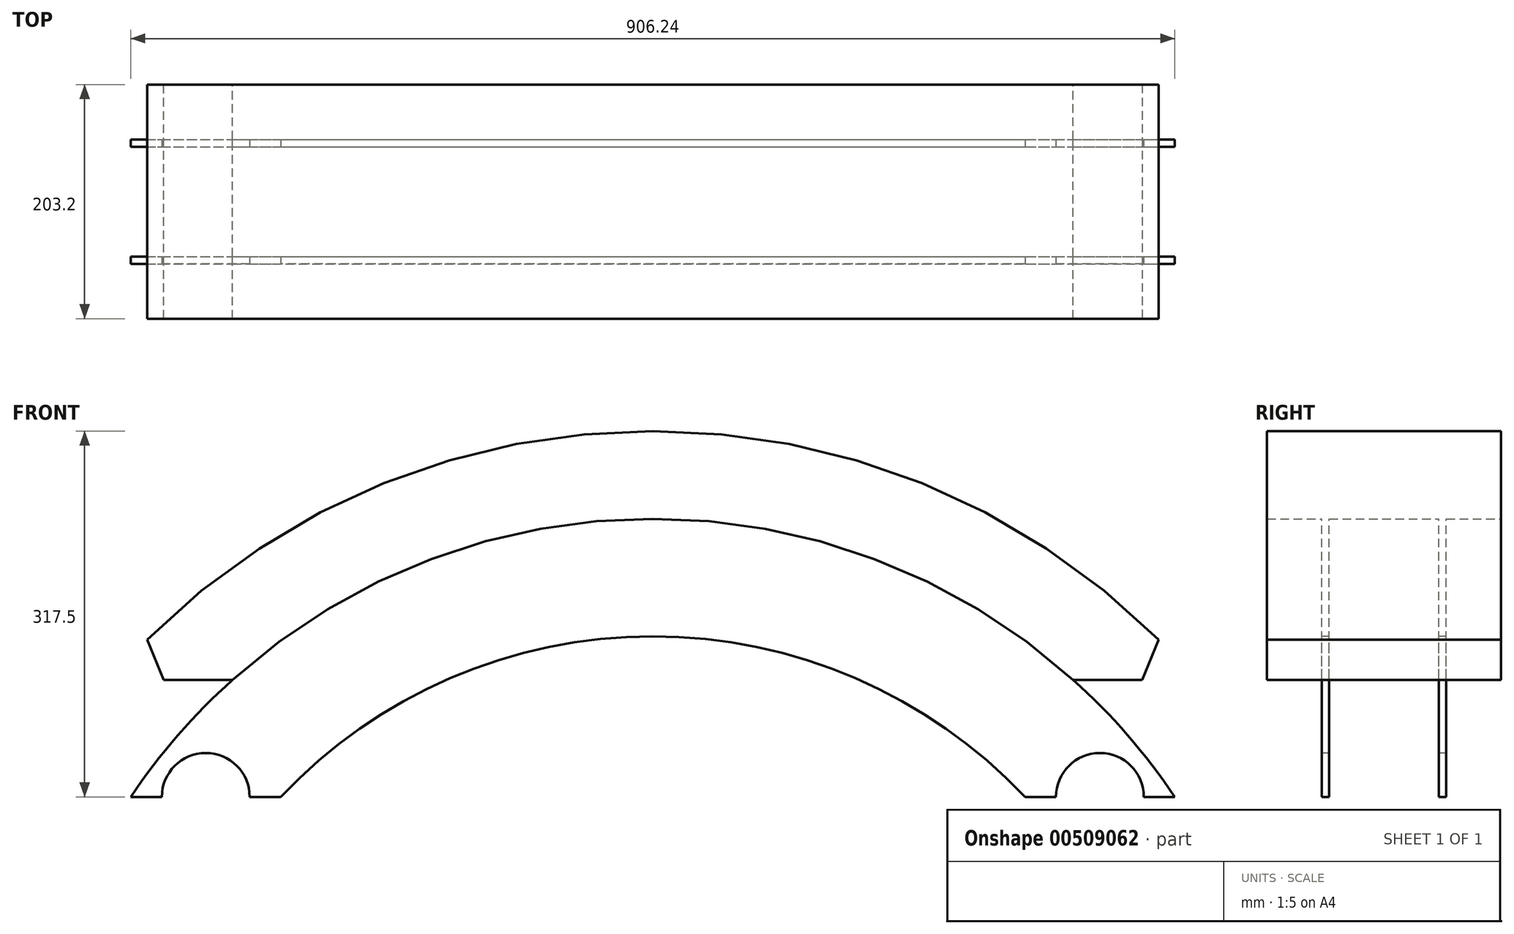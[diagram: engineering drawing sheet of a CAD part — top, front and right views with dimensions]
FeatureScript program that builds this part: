
annotation { "Feature Type Name" : "Feature", "Feature Type Description" : "" }
export const myFeature = defineFeature(function(context is Context, id is Id, definition is map)
    precondition{}
    {
        {
            var Q0;
            Q0=qCreatedBy(makeId("Front.planeOp"),FACE);
            var sketch = newSketch(context, id + "F0", { "sketchPlane" : qUnion([Q0])});
            skCircle(sketch, "E0", {"center": v(0, 0) * mm, "radius": 622.3 * mm});
            skCircle(sketch, "E1", {"center": v(0, 0) * mm, "radius": 546.1 * mm});
            skLineSegment(sketch, "E2.bottom", {"start": v(772.38, 406.4) * mm, "end": v(-772.38, 406.4) * mm});
            skLineSegment(sketch, "E2.top", {"start": v(772.38, -406.4) * mm, "end": v(-772.38, -406.4) * mm});
            skLineSegment(sketch, "E2.left", {"start": v(772.38, 406.4) * mm, "end": v(772.38, -406.4) * mm});
            skLineSegment(sketch, "E2.right", {"start": v(-772.38, 406.4) * mm, "end": v(-772.38, -406.4) * mm});
            skSolve(sketch);
        }
        {
            var Q0;
            {var subQ0=sQuery(id+"F0.wireOp",EDGE,"E2.bottom");var subQ1=sQuery(id+"F0.wireOp",EDGE,"E0");var subQ2=makeQuery(id+"F0.imprint","INTERSECT",VERTEX,{"disambiguationData":[OD(0.0)],"derivedFrom":[subQ1,subQ0]});Q0=makeQuery(id+"F0.imprint","IMPRINT",FACE,{"disambiguationData":[TD([[makeQuery(id+"F0.imprint","IMPRINT",EDGE,{"disambiguationData":[TD([[subQ2,1.0]])],"derivedFrom":subQ1}),1.0]])]});}
            extrude(context, id + "F1", {"entities" : qUnion([Q0]), "depth" : 203.2 * mm});
        }
        {
            var Q0;
            {var subQ0=sQuery(id+"F0.wireOp",EDGE,"E2.bottom");var subQ1=sQuery(id+"F0.wireOp",EDGE,"E0");Q0=makeQuery(id+"F1.opExtrude","SWEPT_EDGE",EDGE,{"disambiguationData":[OSD([subQ1,subQ0]),TDD([makeQuery(id+"F0.imprint","INTERSECT",VERTEX,{"disambiguationData":[OD(0.0)],"derivedFrom":[subQ1,subQ0]})])]});}
            var Q1;
            {var subQ0=sQuery(id+"F0.wireOp",EDGE,"E2.bottom");var subQ1=sQuery(id+"F0.wireOp",EDGE,"E0");Q1=makeQuery(id+"F1.opExtrude","SWEPT_EDGE",EDGE,{"disambiguationData":[OSD([subQ1,subQ0]),TDD([makeQuery(id+"F0.imprint","INTERSECT",VERTEX,{"disambiguationData":[OD(1.0)],"derivedFrom":[subQ1,subQ0]})])]});}
            var Q2;
            {var subQ0=sQuery(id+"F0.wireOp",EDGE,"E2.top");var subQ1=sQuery(id+"F0.wireOp",EDGE,"E0");Q2=makeQuery(id+"F1.opExtrude","SWEPT_EDGE",EDGE,{"disambiguationData":[OSD([subQ1,subQ0]),TDD([makeQuery(id+"F0.imprint","INTERSECT",VERTEX,{"disambiguationData":[OD(0.0)],"derivedFrom":[subQ1,subQ0]})])]});}
            var Q3;
            {var subQ0=sQuery(id+"F0.wireOp",EDGE,"E2.top");var subQ1=sQuery(id+"F0.wireOp",EDGE,"E0");Q3=makeQuery(id+"F1.opExtrude","SWEPT_EDGE",EDGE,{"disambiguationData":[OSD([subQ1,subQ0]),TDD([makeQuery(id+"F0.imprint","INTERSECT",VERTEX,{"disambiguationData":[OD(1.0)],"derivedFrom":[subQ1,subQ0]})])]});}
            chamfer(context, id + "F2", {"entities" : qUnion([Q0, Q1, Q2, Q3]), "width" : 20.32 * mm, "tangentPropagation" : true});
        }
        {
            var Q0;
            Q0=qCreatedBy(makeId("Top.planeOp"),FACE);
            var sketch = newSketch(context, id + "F3", { "sketchPlane" : qUnion([Q0])});
            skLineSegment(sketch, "E3", {"start": v(0, 0) * mm, "end": v(228.6, 0) * mm});
            skLineSegment(sketch, "E4", {"start": v(228.6, 0) * mm, "end": v(228.6, -50.8) * mm});
            skPoint(sketch, "E5.middle", {"position": v(-228.6, -50.8) * mm});
            skLineSegment(sketch, "E6", {"start": v(0, 0) * mm, "end": v(-228.6, 0) * mm});
            skPoint(sketch, "E7.middle", {"position": v(228.6, -50.8) * mm});
            skLineSegment(sketch, "E8", {"start": v(228.6, -152.4) * mm, "end": v(228.6, -203.2) * mm});
            skLineSegment(sketch, "E9", {"start": v(0, 0) * mm, "end": v(0, -50.8) * mm});
            skLineSegment(sketch, "E10", {"start": v(0, -152.4) * mm, "end": v(0, -203.2) * mm});
            skLineSegment(sketch, "E11.bottom", {"start": v(-571.5, -155.58) * mm, "end": v(571.5, -155.58) * mm});
            skLineSegment(sketch, "E11.top", {"start": v(-571.5, -149.23) * mm, "end": v(571.5, -149.23) * mm});
            skLineSegment(sketch, "E11.left", {"start": v(-571.5, -155.58) * mm, "end": v(-571.5, -149.23) * mm});
            skLineSegment(sketch, "E11.right", {"start": v(571.5, -155.58) * mm, "end": v(571.5, -149.23) * mm});
            skPoint(sketch, "E11.middle", {"position": v(0, -152.4) * mm});
            skLineSegment(sketch, "E12.bottom", {"start": v(-571.5, -53.97) * mm, "end": v(571.5, -53.97) * mm});
            skLineSegment(sketch, "E12.top", {"start": v(-571.5, -47.62) * mm, "end": v(571.5, -47.62) * mm});
            skLineSegment(sketch, "E12.left", {"start": v(-571.5, -53.97) * mm, "end": v(-571.5, -47.62) * mm});
            skLineSegment(sketch, "E12.right", {"start": v(571.5, -53.97) * mm, "end": v(571.5, -47.62) * mm});
            skPoint(sketch, "E12.middle", {"position": v(0, -50.8) * mm});
            skSolve(sketch);
        }
        {
            var Q0;
            Q0=makeQuery(id+"F3.imprint","IMPRINT",FACE,{"disambiguationData":[TD([[makeQuery(id+"F3.imprint","IMPRINT",EDGE,{"derivedFrom":sQuery(id+"F3.wireOp",EDGE,"E12.bottom")}),1.0]])]});
            var Q1;
            Q1=makeQuery(id+"F3.imprint","IMPRINT",FACE,{"disambiguationData":[TD([[makeQuery(id+"F3.imprint","IMPRINT",EDGE,{"derivedFrom":sQuery(id+"F3.wireOp",EDGE,"E11.top")}),-1.0]])]});
            var Q2;
            {var subQ0=sQuery(id+"F0.wireOp",EDGE,"E2.bottom");var subQ1=sQuery(id+"F0.wireOp",EDGE,"E1");Q2=makeQuery(id+"F1.opExtrude","SWEPT_FACE",FACE,{"disambiguationData":[OSD([subQ1]),TDD([makeQuery(id+"F0.imprint","IMPRINT",EDGE,{"disambiguationData":[TD([[makeQuery(id+"F0.imprint","INTERSECT",VERTEX,{"disambiguationData":[OD(0.0)],"derivedFrom":[subQ1,subQ0]}),1.0]])],"derivedFrom":subQ1})])]});}
            extrude(context, id + "F4", {"entities" : qUnion([Q0, Q1]), "operationType" : NewBodyOperationType.ADD, "endBound" : BoundingType.UP_TO_SURFACE, "endBoundEntityFace" : qUnion([Q2]), "depth" : 25.4 * mm, "hasSecondDirection" : true, "secondDirectionOppositeDirection" : true, "secondDirectionDepth" : -304.8 * mm});
        }
        {
            var Q0;
            Q0=makeQuery(id+"F4.opExtrude","SWEPT_FACE",FACE,{"disambiguationData":[OSD([sQuery(id+"F3.wireOp",EDGE,"E11.bottom")])]});
            var sketch = newSketch(context, id + "F5", { "sketchPlane" : qUnion([Q0])});
            skCircle(sketch, "E13", {"center": v(0, 0) * mm, "radius": 444.09 * mm});
            skSolve(sketch);
        }
        {
            var Q0;
            {var subQ0=sQuery(id+"F5.wireOp",EDGE,"E13");var subQ1=makeQuery(id+"F4.opExtrude","CAP_EDGE",EDGE,{"disambiguationData":[OSD([sQuery(id+"F3.wireOp",EDGE,"E11.bottom")])],"isStart":true});var subQ2=makeQuery(id+"F5.imprint","INTERSECT",VERTEX,{"disambiguationData":[OD(0.0)],"derivedFrom":[subQ1,subQ0]});Q0=makeQuery(id+"F5.imprint","IMPRINT",FACE,{"disambiguationData":[TD([[makeQuery(id+"F5.imprint","IMPRINT",EDGE,{"disambiguationData":[TD([[subQ2,1.0]])],"derivedFrom":subQ0}),1.0]])]});}
            extrude(context, id + "F6", {"entities" : qUnion([Q0]), "operationType" : NewBodyOperationType.REMOVE, "oppositeDirection" : true, "depth" : 127 * mm});
        }
        {
            var Q0;
            Q0=makeQuery(id+"F4.opExtrude","SWEPT_FACE",FACE,{"disambiguationData":[OSD([sQuery(id+"F3.wireOp",EDGE,"E11.bottom")])]});
            var sketch = newSketch(context, id + "F7", { "sketchPlane" : qUnion([Q0])});
            skCircle(sketch, "E14", {"center": v(-388.05, 304.8) * mm, "radius": 38.1 * mm});
            skCircle(sketch, "E15", {"center": v(388.05, 304.8) * mm, "radius": 38.1 * mm});
            skSolve(sketch);
        }
        {
            var Q0;
            {var subQ0=sQuery(id+"F7.wireOp",EDGE,"E14");var subQ1=makeQuery(id+"F6.boolean.opBoolean","SPLIT",EDGE,{"disambiguationData":[OD(0.0)],"derivedFrom":makeQuery(id+"F4.opExtrude","CAP_EDGE",EDGE,{"disambiguationData":[OSD([sQuery(id+"F3.wireOp",EDGE,"E11.bottom")])],"isStart":true})});var subQ2=makeQuery(id+"F7.imprint","INTERSECT",VERTEX,{"disambiguationData":[OD(0.0)],"derivedFrom":[subQ1,subQ0]});Q0=makeQuery(id+"F7.imprint","IMPRINT",FACE,{"disambiguationData":[TD([[makeQuery(id+"F7.imprint","IMPRINT",EDGE,{"disambiguationData":[TD([[subQ2,1.0]])],"derivedFrom":subQ0}),1.0]])]});}
            var Q1;
            {var subQ0=sQuery(id+"F7.wireOp",EDGE,"E15");var subQ1=makeQuery(id+"F6.boolean.opBoolean","SPLIT",EDGE,{"disambiguationData":[OD(1.0)],"derivedFrom":makeQuery(id+"F4.opExtrude","CAP_EDGE",EDGE,{"disambiguationData":[OSD([sQuery(id+"F3.wireOp",EDGE,"E11.bottom")])],"isStart":true})});var subQ2=makeQuery(id+"F7.imprint","INTERSECT",VERTEX,{"disambiguationData":[OD(0.0)],"derivedFrom":[subQ1,subQ0]});Q1=makeQuery(id+"F7.imprint","IMPRINT",FACE,{"disambiguationData":[TD([[makeQuery(id+"F7.imprint","IMPRINT",EDGE,{"disambiguationData":[TD([[subQ2,-1.0]])],"derivedFrom":subQ0}),1.0]])]});}
            extrude(context, id + "F8", {"entities" : qUnion([Q0, Q1]), "operationType" : NewBodyOperationType.REMOVE, "oppositeDirection" : true, "depth" : 127 * mm});
        }
    });
